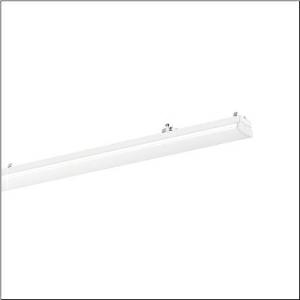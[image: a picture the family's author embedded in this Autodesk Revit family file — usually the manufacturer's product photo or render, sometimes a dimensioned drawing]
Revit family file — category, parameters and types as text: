
# Revit family: licross_r__11_recessed_opal_mo_51tl1ddn495g_fb0a
name_source: partatom
category: Lighting Fixtures
units: mm (PartAtom-declared; Revit-internal decimal feet)

## family parameters
Cut with Voids When Loaded = No
Host = Face
Light Source = No
Part Type = Normal
Room Calculation Point = No
Round Connector Dimension = Use Diameter
Shared = No

## types (1)
- --- (1 x LED, 9710 lm, 56.7 W, 4000K)
    Apparent Load = 57 VA
    CIE Flux Codes = 44 73 91 87 100
    Color Rendering = 80
    Color Temperature = 4000K
    Default Elevation = 1800 mm
    Description = Licross® 11 recessed opal MO, luminaire insert, of sheet steel, coil coated, white, length: 1.500mm, width: 76mm, height: 87mm, LED rated luminous flux: 9.710lm, light colour: 840, control gear: DALI 2, with plug, 5-pole, with phase selection, mains connection: 220..240V, AC, 50/60Hz, rated input power: 57W, internal wiring halogen-free, primary optical cover: cover, of PMMA, light emission: direct with ceiling illumination distribution, primary light characteristic: symmetric, protection rating (complete): IP40, insulation class (complete): insulation class I (protective earthing), certification: CE, ENEC, VDE, UKCA, protection symbol: D if used in an environment without relevant dust loads with corresponding accessories, impact resistance: IK06, permissible ambient temperature for indoor applications: -25..+35°C, corresponds to IFS (International Featured Standards) requirements for safety and quality in the food industry, reducing of maximum allowable ambient temperature of 5°C with ceiling mounting, LABS conformity tested according to VDMA 24364:2018-05, packaging unit: 1 piece
    Height = 83 mm
    Lamp = 1 x LED
    Lamp Light Flux = 9710 lm
    Lamp Power = 56.7 W
    Lamp count = 1
    Length = 1500 mm
    Luminous efficacy = 171 lm/W
    Manufacturer = Siteco
    ModVariant = No
    Model = 51TL1DDN495G
    Mounting Place = Ceiling
    Mounting Type = Pendant
    Number of Poles = 1
    OnlyDefault = Yes
    Power Factor = 1
    Product Name = Licross® 11 recessed opal MO
    Product group = luminaire insert | ceiling pendant
    ProductGroupID = 902
    Protection Class = Protection class I
    Protection Degree = IP 40
    RLX_Detail_Level = 1
    RLX_Emergency_Light_Flux = 0 lm
    RLX_Emergency_Type = 0
    RLX_Emergency_Type_DB = No
    RlxData = <blob elided: 26857 chars, md5=33bde639>
    Socket = socket
    Standby Power = 0 W
    System Light Flux = 9710 lm
    System Power = 57 W
    Type Comments = factory setting: luminous flux: 100 % | dim-lin: 254 | 378 mA
    Type Image = l_1313666.jpg
    URL = http://relux.com
    VarID = @adj_097671
    Voltage = 0 V
    Weight = 0.00 kg
    Width = 76 mm

## geometry (parser evidence)
native form markers: Blend x4, Sweep x12
no freeform markers — native parametric forms only
